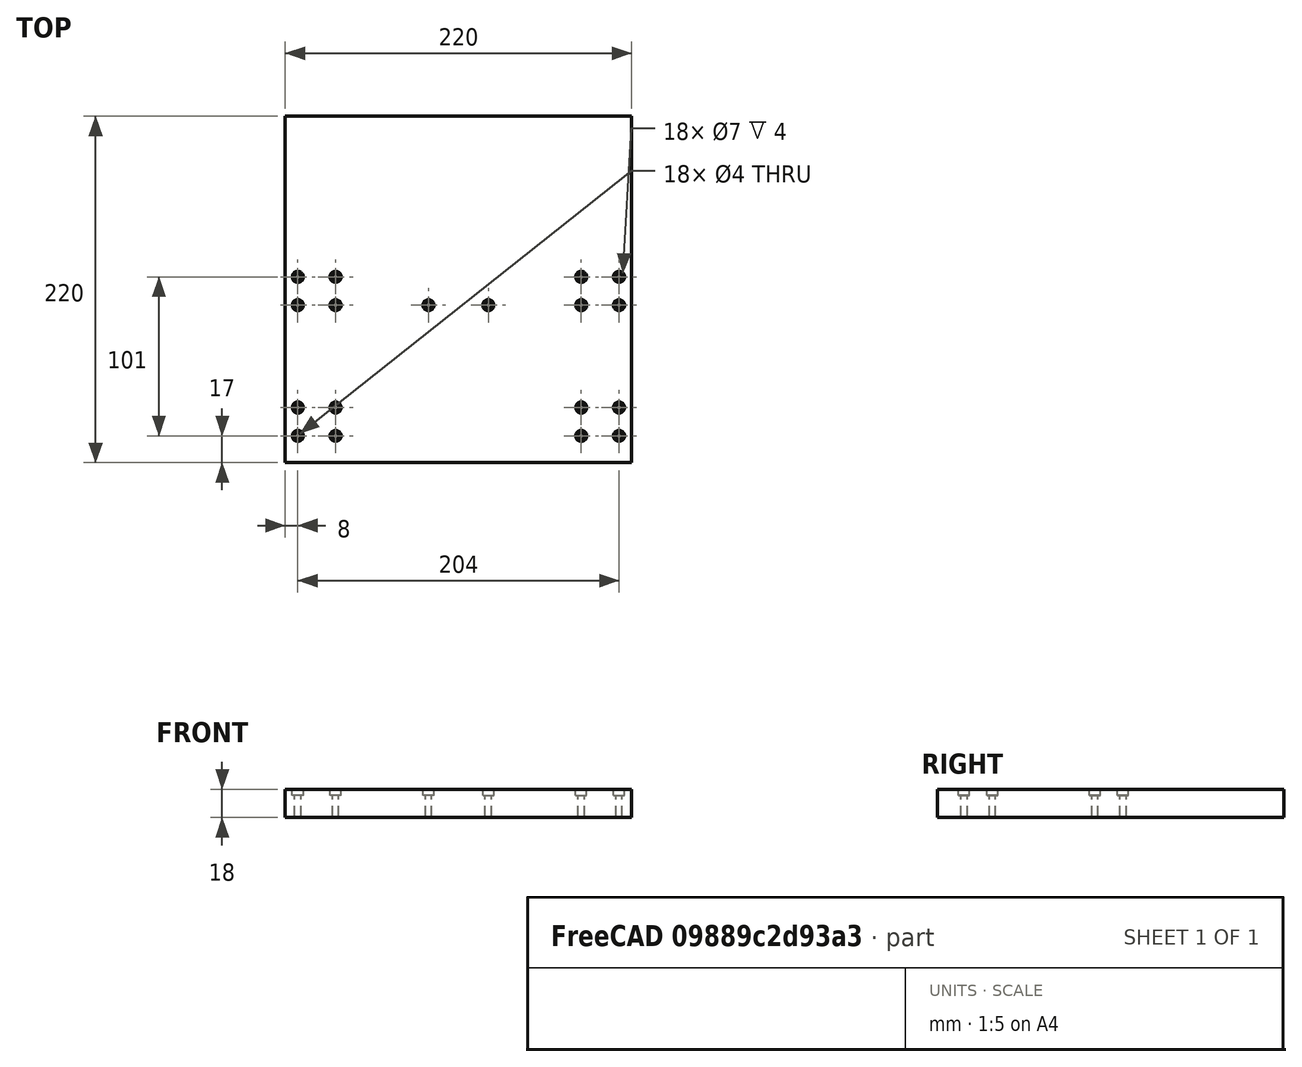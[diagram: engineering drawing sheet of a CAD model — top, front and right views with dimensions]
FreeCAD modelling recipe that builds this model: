
FCSTD DOCUMENT  (FreeCAD 0.17R13541 (Git))
Label: Base-Mesa
License: All rights reserved
LicenseURL: http://en.wikipedia.org/wiki/All_rights_reserved
objects: Part::Cylinder×18, Part::MultiFuse×17, Part::Box×1, Part::Cut×1, Part::Mirroring×1
note: 38 computed .brp shape members not serialized (recipe doc carries the construction recipe); baked Part::Feature solids carry a one-line shape summary decoded from their .brp

FEATURE [Part::Box] Box  label="Cubo"
  AttacherType = Attacher::AttachEngine3D
  Height = 18
  Length = 110
  Width = 220
FEATURE [Part::Cylinder] Cylinder  label="Cilindro"
  Angle = 360
  AttacherType = Attacher::AttachEngine3D
  Height = 25
  Placement = pos=(8,17,0) rot=(0,0,1;0rad)
  Radius = 2
FEATURE [Part::Cylinder] Cylinder001  label="Cilindro001"
  Angle = 360
  AttacherType = Attacher::AttachEngine3D
  Height = 8
  Placement = pos=(8,17,14) rot=(0,0,1;0rad)
  Radius = 3.5
FEATURE [Part::MultiFuse] Fusion
  Refine = true
  Shapes = -> [Cylinder,Cylinder001]
FEATURE [Part::Cylinder] Cylinder002  label="Cilindro002"
  Angle = 360
  AttacherType = Attacher::AttachEngine3D
  Height = 8
  Placement = pos=(8,17,14) rot=(0,0,1;0rad)
  Radius = 3.5
FEATURE [Part::Cylinder] Cylinder003  label="Cilindro003"
  Angle = 360
  AttacherType = Attacher::AttachEngine3D
  Height = 25
  Placement = pos=(8,17,0) rot=(0,0,1;0rad)
  Radius = 2
FEATURE [Part::MultiFuse] Fusion001
  Placement = pos=(24,0,0) rot=(0,0,1;0rad)
  Refine = true
  Shapes = -> [Cylinder003,Cylinder002]
FEATURE [Part::Cylinder] Cylinder004  label="Cilindro004"
  Angle = 360
  AttacherType = Attacher::AttachEngine3D
  Height = 25
  Placement = pos=(8,17,0) rot=(0,0,1;0rad)
  Radius = 2
FEATURE [Part::Cylinder] Cylinder005  label="Cilindro005"
  Angle = 360
  AttacherType = Attacher::AttachEngine3D
  Height = 8
  Placement = pos=(8,17,14) rot=(0,0,1;0rad)
  Radius = 3.5
FEATURE [Part::MultiFuse] Fusion002
  Placement = pos=(83,83,0) rot=(0,0,1;0rad)
  Refine = true
  Shapes = -> [Cylinder004,Cylinder005]
FEATURE [Part::MultiFuse] Fusion003
  Refine = true
  Shapes = -> [Fusion,Fusion001]
FEATURE [Part::Cylinder] Cylinder006  label="Cilindro006"
  Angle = 360
  AttacherType = Attacher::AttachEngine3D
  Height = 25
  Placement = pos=(8,17,0) rot=(0,0,1;0rad)
  Radius = 2
FEATURE [Part::Cylinder] Cylinder007  label="Cilindro007"
  Angle = 360
  AttacherType = Attacher::AttachEngine3D
  Height = 8
  Placement = pos=(8,17,14) rot=(0,0,1;0rad)
  Radius = 3.5
FEATURE [Part::Cylinder] Cylinder008  label="Cilindro008"
  Angle = 360
  AttacherType = Attacher::AttachEngine3D
  Height = 8
  Placement = pos=(8,17,14) rot=(0,0,1;0rad)
  Radius = 3.5
FEATURE [Part::Cylinder] Cylinder009  label="Cilindro009"
  Angle = 360
  AttacherType = Attacher::AttachEngine3D
  Height = 25
  Placement = pos=(8,17,0) rot=(0,0,1;0rad)
  Radius = 2
FEATURE [Part::MultiFuse] Fusion005
  Refine = true
  Shapes = -> [Cylinder009,Cylinder008]
FEATURE [Part::MultiFuse] Fusion006
  Placement = pos=(24,0,0) rot=(0,0,1;0rad)
  Refine = true
  Shapes = -> [Cylinder006,Cylinder007]
FEATURE [Part::MultiFuse] Fusion004
  Placement = pos=(0,18,0) rot=(0,0,1;0rad)
  Refine = true
  Shapes = -> [Fusion005,Fusion006]
FEATURE [Part::MultiFuse] Fusion007
  Refine = true
  Shapes = -> [Fusion004,Fusion003]
FEATURE [Part::Cylinder] Cylinder010  label="Cilindro010"
  Angle = 360
  AttacherType = Attacher::AttachEngine3D
  Height = 25
  Placement = pos=(8,17,0) rot=(0,0,1;0rad)
  Radius = 2
FEATURE [Part::Cylinder] Cylinder011  label="Cilindro011"
  Angle = 360
  AttacherType = Attacher::AttachEngine3D
  Height = 8
  Placement = pos=(8,17,14) rot=(0,0,1;0rad)
  Radius = 3.5
FEATURE [Part::Cylinder] Cylinder012  label="Cilindro012"
  Angle = 360
  AttacherType = Attacher::AttachEngine3D
  Height = 8
  Placement = pos=(8,17,14) rot=(0,0,1;0rad)
  Radius = 3.5
FEATURE [Part::Cylinder] Cylinder013  label="Cilindro013"
  Angle = 360
  AttacherType = Attacher::AttachEngine3D
  Height = 25
  Placement = pos=(8,17,0) rot=(0,0,1;0rad)
  Radius = 2
FEATURE [Part::Cylinder] Cylinder014  label="Cilindro014"
  Angle = 360
  AttacherType = Attacher::AttachEngine3D
  Height = 25
  Placement = pos=(8,17,0) rot=(0,0,1;0rad)
  Radius = 2
FEATURE [Part::Cylinder] Cylinder015  label="Cilindro015"
  Angle = 360
  AttacherType = Attacher::AttachEngine3D
  Height = 8
  Placement = pos=(8,17,14) rot=(0,0,1;0rad)
  Radius = 3.5
FEATURE [Part::MultiFuse] Fusion009
  Placement = pos=(24,0,0) rot=(0,0,1;0rad)
  Refine = true
  Shapes = -> [Cylinder014,Cylinder015]
FEATURE [Part::Cylinder] Cylinder016  label="Cilindro016"
  Angle = 360
  AttacherType = Attacher::AttachEngine3D
  Height = 25
  Placement = pos=(8,17,0) rot=(0,0,1;0rad)
  Radius = 2
FEATURE [Part::Cylinder] Cylinder017  label="Cilindro017"
  Angle = 360
  AttacherType = Attacher::AttachEngine3D
  Height = 8
  Placement = pos=(8,17,14) rot=(0,0,1;0rad)
  Radius = 3.5
FEATURE [Part::MultiFuse] Fusion011
  Refine = true
  Shapes = -> [Cylinder016,Cylinder017]
FEATURE [Part::MultiFuse] Fusion010
  Placement = pos=(0,18,0) rot=(0,0,1;0rad)
  Refine = true
  Shapes = -> [Fusion011,Fusion009]
FEATURE [Part::MultiFuse] Fusion013
  Refine = true
  Shapes = -> [Cylinder013,Cylinder012]
FEATURE [Part::MultiFuse] Fusion014
  Placement = pos=(24,0,0) rot=(0,0,1;0rad)
  Refine = true
  Shapes = -> [Cylinder010,Cylinder011]
FEATURE [Part::MultiFuse] Fusion012
  Refine = true
  Shapes = -> [Fusion013,Fusion014]
FEATURE [Part::MultiFuse] Fusion008
  Placement = pos=(0,83,0) rot=(0,0,1;0rad)
  Refine = true
  Shapes = -> [Fusion010,Fusion012]
FEATURE [Part::MultiFuse] Fusion015
  Refine = true
  Shapes = -> [Fusion008,Fusion007,Fusion002]
FEATURE [Part::Cut] Cut
  Base = -> Box
  Refine = true
  Tool = -> Fusion015
FEATURE [Part::Mirroring] mirror  label="Mirror of Cut"
  Base = (110,0,0)
  Normal = (0.97,0,0)
  Source = -> Cut
FEATURE [Part::MultiFuse] Fusion016
  Refine = true
  Shapes = -> [mirror,Cut]
